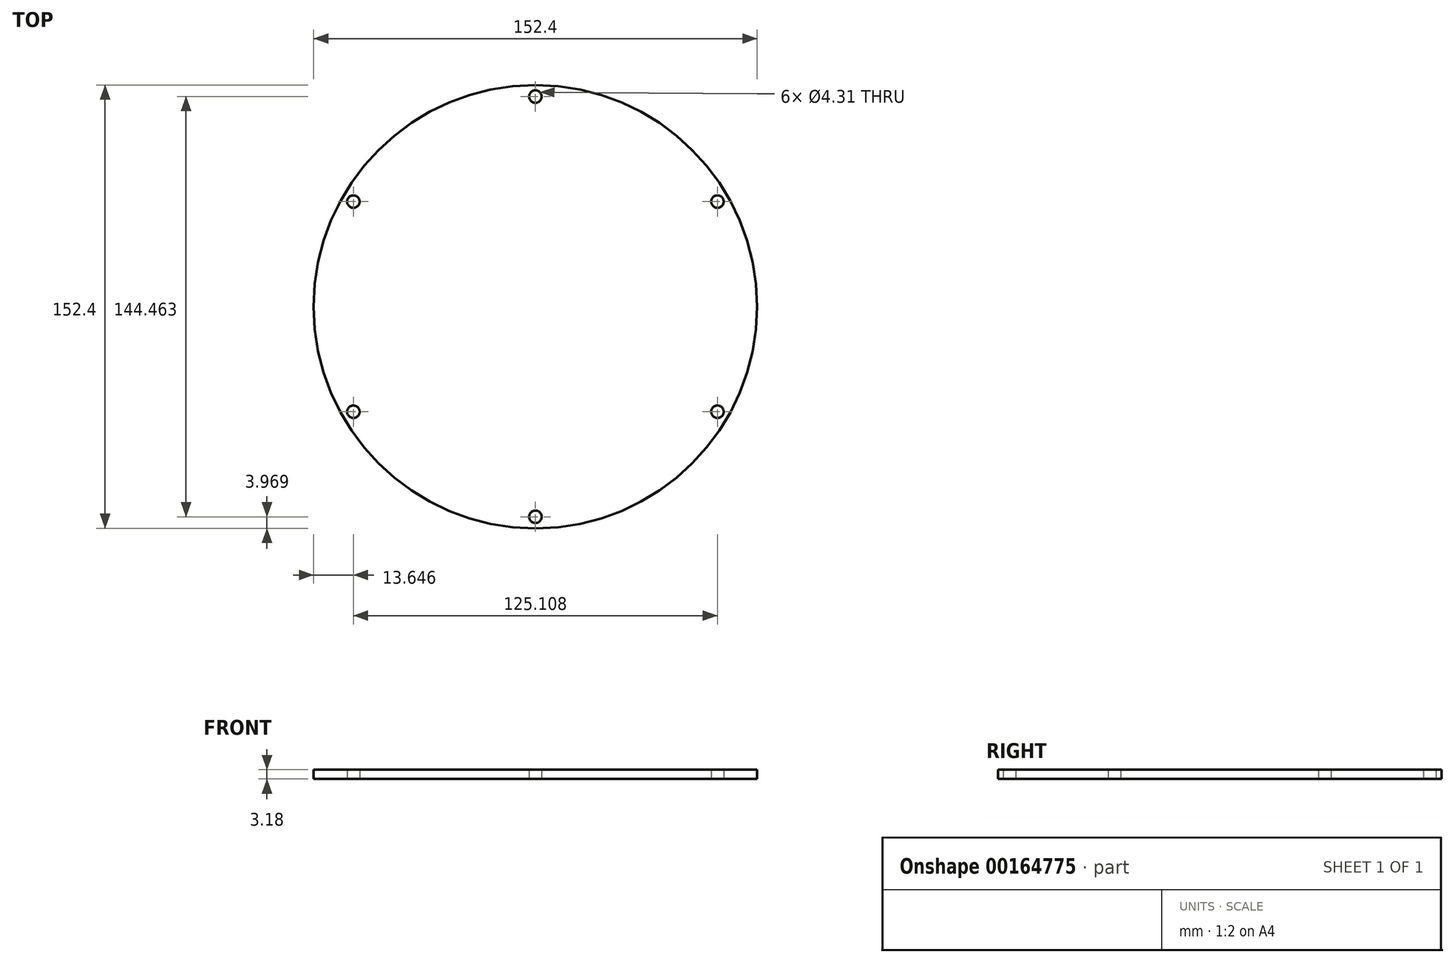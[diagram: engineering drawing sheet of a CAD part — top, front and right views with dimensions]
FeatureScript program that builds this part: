
annotation { "Feature Type Name" : "Feature", "Feature Type Description" : "" }
export const myFeature = defineFeature(function(context is Context, id is Id, definition is map)
    precondition{}
    {
        {
            var Q0;
            Q0=qCreatedBy(makeId("Top.planeOp"),FACE);
            var sketch = newSketch(context, id + "F0", { "sketchPlane" : qUnion([Q0])});
            skCircle(sketch, "E0", {"center": v(0, 0) * mm, "radius": 76.2 * mm});
            skCircle(sketch, "E1.cCircle", {"center": v(0, 0) * mm, "radius": 62.55 * mm, "construction": true});
            skLineSegment(sketch, "E1.0", {"start": v(-62.55, -36.12) * mm, "end": v(-62.55, 36.12) * mm, "construction": true});
            skLineSegment(sketch, "E1.1", {"start": v(-62.55, 36.12) * mm, "end": v(0, 72.23) * mm, "construction": true});
            skLineSegment(sketch, "E1.2", {"start": v(0, 72.23) * mm, "end": v(62.55, 36.12) * mm, "construction": true});
            skLineSegment(sketch, "E1.3", {"start": v(62.55, 36.12) * mm, "end": v(62.55, -36.12) * mm, "construction": true});
            skLineSegment(sketch, "E1.4", {"start": v(62.55, -36.12) * mm, "end": v(0, -72.23) * mm, "construction": true});
            skLineSegment(sketch, "E1.5", {"start": v(0, -72.23) * mm, "end": v(-62.55, -36.12) * mm, "construction": true});
            skPoint(sketch, "E1.0.midPoint", {"position": v(-62.55, 0) * mm});
            skCircle(sketch, "E2", {"center": v(-62.55, -36.12) * mm, "radius": 3.97 * mm, "construction": true});
            skCircle(sketch, "E3", {"center": v(-62.55, -36.12) * mm, "radius": 2.15 * mm});
            skCircle(sketch, "E4", {"center": v(-62.55, 36.12) * mm, "radius": 2.15 * mm});
            skCircle(sketch, "E5", {"center": v(0, -72.23) * mm, "radius": 2.15 * mm});
            skCircle(sketch, "E6", {"center": v(62.55, -36.12) * mm, "radius": 2.15 * mm});
            skCircle(sketch, "E7", {"center": v(62.55, 36.12) * mm, "radius": 2.15 * mm});
            skCircle(sketch, "E8", {"center": v(0, 72.23) * mm, "radius": 2.15 * mm});
            skSolve(sketch);
        }
        {
            var Q0;
            Q0 = qSketchRegion(id + "F0", true);
            extrude(context, id + "F1", {"entities" : qUnion([Q0]), "depth" : 3.17 * mm});
        }
    });
